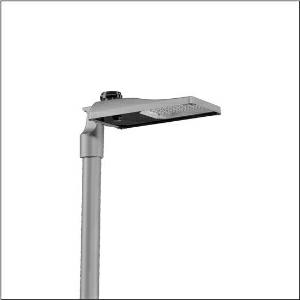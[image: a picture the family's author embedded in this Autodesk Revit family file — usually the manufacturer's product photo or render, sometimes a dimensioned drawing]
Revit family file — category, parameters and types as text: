
# Revit family: streetlight_sl_31_mini___st1_0a_5xh6d35m08ja_363a
name_source: partatom
category: Lighting Fixtures
units: mm (PartAtom-declared; Revit-internal decimal feet)

## family parameters
Cut with Voids When Loaded = No
Host = Face
Light Source = No
Part Type = Normal
Room Calculation Point = No
Round Connector Dimension = Use Diameter
Shared = No

## types (1)
- --- (1 x LED, 12270 lm, 82.5 W, 3000K)
    Apparent Load = 83 VA
    CIE Flux Codes = 40 73 97 100 100
    Color Rendering = 70
    Color Temperature = 3000K
    Default Elevation = 1800 mm
    Description = Streetlight SL 31 mini NEMA (7pin), Desk-Remote mast luminaire for post-top, side-entry; light control with lens of PMMA; light distribution: ST1.0a, direct asymmetric distribution, for standard-compliant lighting for roads and squares; LED: luminous flux: 12.270lm, light colour: 730, colour temperature: 3000K; luminous efficacy: 148,7lm/W; control: pre-setting: linear dimming characteristic, flexible luminous flux parameterisation, time-dependent luminous flux control, constant luminous flux control, intelligent temperature release in ECG and LED module, overheat protection; luminaire housing, of diecast aluminium, Siteco® metallic grey (DB 702S), corrosivity category C5 high according to DIN EN ISO 12944; cover of toughened safety glass, transparent, opened without tools; mast flange of diecast aluminium, Siteco® metallic grey (DB 702S), spigot size: 76/60mm, mast flange included unmounted; with cable H07RN-F 3x 1.5mm², cable length: 10,5m, connection cable pre-assembled; mains connection: 220..240V, AC, 50/60Hz; power consumption (at start of service life): 82,5W / (at end of service life): 90,1W / (with reduced operation 50%): 36,8W; protection rating (complete): IP66; insulation class (complete): insulation class I (protective earthing); impact resistance: IK09; certification: CE, ENEC, ENEC+, VDE, UKCA; permissible operating ambient temperature for outdoor applications: -40..+50°C; packaging unit: 1 piece

Light Distribution: ST1.0a
    Height = 76 mm
    Lamp = 1 x LED
    Lamp Light Flux = 12270 lm
    Lamp Power = 82.5 W
    Lamp count = 1
    Length = 547 mm
    Luminous efficacy = 149 lm/W
    Manufacturer = Siteco
    ModVariant = No
    Model = 5XH6D35M08JA
    Number of Poles = 1
    OnlyDefault = Yes
    Power Factor = 1
    Product Name = Streetlight SL 31 mini | ST1.0a
    Product group = mast luminaire | pylon top
    ProductGroupID = 6100
    Protection Class = Protection class I
    Protection Degree = IP 66
    RLX_Detail_Level = 1
    RLX_Emergency_Light_Flux = 0 lm
    RLX_Emergency_Type = 0
    RLX_Emergency_Type_DB = No
    RlxData = <blob elided: 40461 chars, md5=3ad988e3>
    Socket = socket
    Standby Power = 0 W
    System Light Flux = 12270 lm
    System Power = 83 W
    Type Comments = factory setting: luminous flux: 100 % | dim-lin: 254 | 870 mA
    Type Image = l_1300324.jpg
    URL = http://relux.com
    VarID = @adj_050046
    Voltage = 0 V
    Weight = 0.00 kg
    Width = 265 mm

## geometry (parser evidence)
native form markers: Blend x4, Sweep x9
no freeform markers — native parametric forms only
